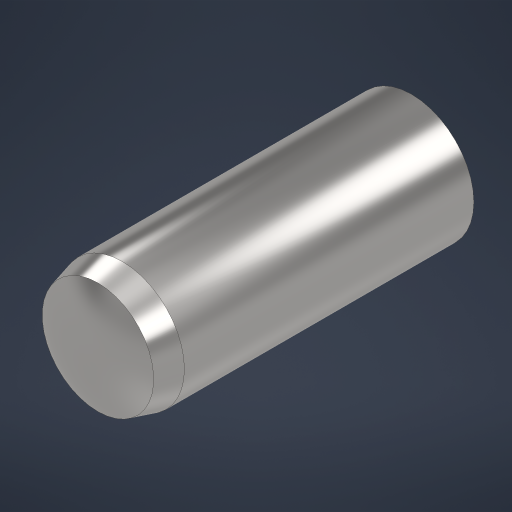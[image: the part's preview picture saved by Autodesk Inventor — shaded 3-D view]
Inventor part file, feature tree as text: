
AUTODESK INVENTOR PART (.ipt)
format: ipt  version: 2024 (Build 280153000, 153)  size: 217,600 bytes
history: native  units: in
note: dims shown in document units (in); Inventor stores cm internally (conversion verified against a paired STEP export)
features: revolve x1
ambient origin geometry x8: Origin, YZ Plane, XZ Plane, XY Plane, X Axis, Y Axis, Z Axis, Center Point
bodies: Solid1 (feature_tree)
feature tree (1):
  revolve  "Revolve1"  [1 undecoded]
note: 1 required parameter value undecoded (feature->parameter linkage not recoverable at this tier; creation-order binding heuristic only, values carry confidence <= 0.55)
